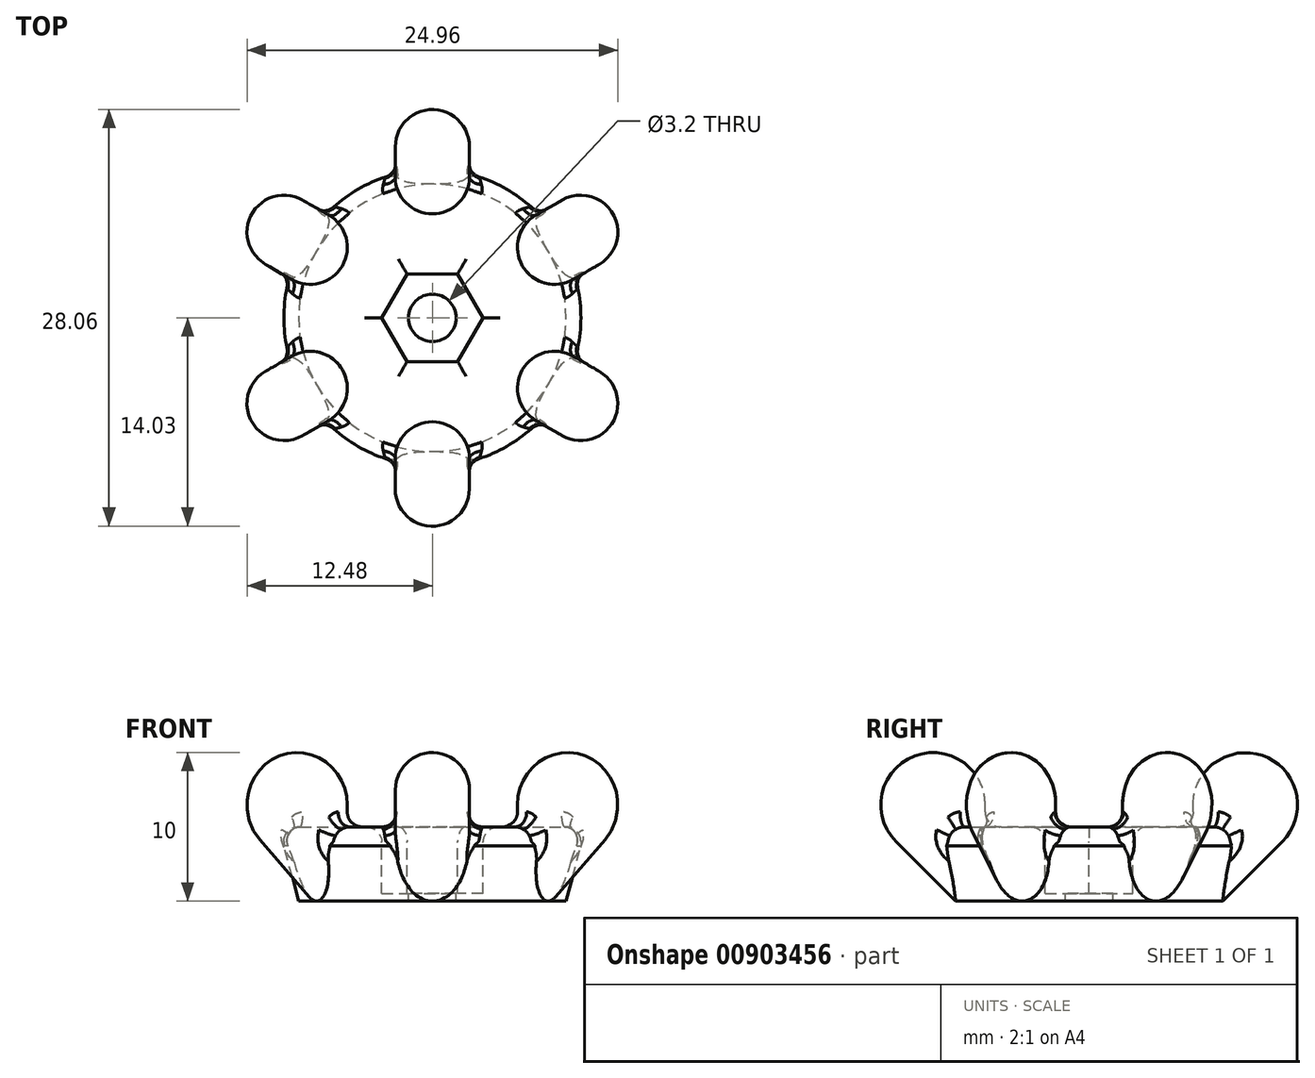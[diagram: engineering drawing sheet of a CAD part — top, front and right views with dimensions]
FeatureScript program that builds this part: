
annotation { "Feature Type Name" : "Feature", "Feature Type Description" : "" }
export const myFeature = defineFeature(function(context is Context, id is Id, definition is map)
    precondition{}
    {
        {
            var Q0;
            Q0=qCreatedBy(makeId("Top.planeOp"),FACE);
            var sketch = newSketch(context, id + "F0", { "sketchPlane" : qUnion([Q0])});
            skCircle(sketch, "E0", {"center": v(0, 0) * mm, "radius": 10 * mm});
            skLineSegment(sketch, "E1", {"start": v(0, 0) * mm, "end": v(0, 13.6) * mm, "construction": true});
            skSolve(sketch);
        }
        {
            var Q0;
            Q0=makeQuery(id+"F0.imprint","IMPRINT",FACE,{"disambiguationData":[TD([[makeQuery(id+"F0.imprint","IMPRINT",EDGE,{"derivedFrom":sQuery(id+"F0.wireOp",EDGE,"E0")}),1.0]])]});
            var Q1;
            Q1=sQuery(id+"F0.wireOp",EDGE,"E1");
            var Q2;
            Q2=sQuery(id+"F0.wireOp",EDGE,"E0");
            extrude(context, id + "F1", {"entities" : qUnion([Q0]), "surfaceEntities" : qUnion([Q1, Q2]), "depth" : 5 * mm, "offsetDistance" : 25 * mm});
        }
        {
            var Q0;
            Q0=makeQuery(id+"F1.opExtrude","CAP_EDGE",EDGE,{"disambiguationData":[OSD([sQuery(id+"F0.wireOp",EDGE,"E0")])],"isStart":true});
            chamfer(context, id + "F2", {"entities" : qUnion([Q0]), "chamferType" : ChamferType.OFFSET_ANGLE, "width" : 1 * mm, "oppositeDirection" : true, "angle" : 75 * degree, "tangentPropagation" : true});
        }
        {
            var Q0;
            Q0=makeQuery(id+"F1.opExtrude","CAP_EDGE",EDGE,{"disambiguationData":[OSD([sQuery(id+"F0.wireOp",EDGE,"E0")])],"isStart":false});
            fillet(context, id + "F3", {"entities" : qUnion([Q0]), "radius" : 1 * mm, "tangentPropagation" : true, "allowEdgeOverflow" : false});
        }
        {
            var Q0;
            Q0=makeQuery(id+"F1.opExtrude","CAP_FACE",FACE,{"disambiguationData":[OSD([sQuery(id+"F0.wireOp",EDGE,"E0")])],"isStart":false});
            var sketch = newSketch(context, id + "F4", { "sketchPlane" : qUnion([Q0])});
            skCircle(sketch, "E2.cCircle", {"center": v(0, 0) * mm, "radius": 2.95 * mm, "construction": true});
            skLineSegment(sketch, "E2.0", {"start": v(-1.7, 2.95) * mm, "end": v(1.7, 2.95) * mm});
            skLineSegment(sketch, "E2.1", {"start": v(1.7, 2.95) * mm, "end": v(3.4, 0) * mm});
            skLineSegment(sketch, "E2.2", {"start": v(3.4, 0) * mm, "end": v(1.7, -2.95) * mm});
            skLineSegment(sketch, "E2.3", {"start": v(1.7, -2.95) * mm, "end": v(-1.7, -2.95) * mm});
            skLineSegment(sketch, "E2.4", {"start": v(-1.7, -2.95) * mm, "end": v(-3.4, 0) * mm});
            skLineSegment(sketch, "E2.5", {"start": v(-3.4, 0) * mm, "end": v(-1.7, 2.95) * mm});
            skPoint(sketch, "E2.0.midPoint", {"position": v(0, 2.95) * mm});
            skCircle(sketch, "E3", {"center": v(0, 0) * mm, "radius": 1.6 * mm});
            skSolve(sketch);
        }
        {
            var Q0;
            Q0=qSketchRegion(id+"F4",true);
            var Q1;
            Q1=makeQuery(id+"F4.imprint","IMPRINT",FACE,{"disambiguationData":[TD([[makeQuery(id+"F4.imprint","IMPRINT",EDGE,{"derivedFrom":sQuery(id+"F4.wireOp",EDGE,"E3")}),1.0]])]});
            extrude(context, id + "F5", {"entities" : qUnion([Q0, Q1]), "operationType" : NewBodyOperationType.REMOVE, "oppositeDirection" : true, "depth" : (5 - 0.5) * mm, "offsetDistance" : 25 * mm});
        }
        {
            var Q0;
            Q0=makeQuery(id+"F4.imprint","IMPRINT",FACE,{"disambiguationData":[TD([[makeQuery(id+"F4.imprint","IMPRINT",EDGE,{"derivedFrom":sQuery(id+"F4.wireOp",EDGE,"E3")}),1.0]])]});
            var Q1;
            Q1=sQuery(id+"F4.wireOp",EDGE,"E3");
            extrude(context, id + "F6", {"entities" : qUnion([Q0]), "operationType" : NewBodyOperationType.REMOVE, "surfaceEntities" : qUnion([Q1]), "oppositeDirection" : true, "depth" : 25 * mm, "offsetDistance" : 25 * mm});
        }
        {
            var Q0;
            Q0=qCreatedBy(makeId("Right.planeOp"),FACE);
            var sketch = newSketch(context, id + "F7", { "sketchPlane" : qUnion([Q0])});
            skLineSegment(sketch, "E4", {"start": v(9, 0) * mm, "end": v(13, 4) * mm});
            skLineSegment(sketch, "E5", {"start": v(7, 2.8) * mm, "end": v(9, 0) * mm});
            skLineSegment(sketch, "E6", {"start": v(-9, 0) * mm, "end": v(-10, 3.73) * mm});
            skLineSegment(sketch, "E7", {"start": v(7, 6.49) * mm, "end": v(7, 2.8) * mm});
            skArc(sketch, "E8", {"start": v(13, 4) * mm, "mid": v(11.86, 9.73) * mm, "end": v(7, 6.49) * mm});
            skLineSegment(sketch, "E9", {"start": v(10, 3.73) * mm, "end": v(9, 0) * mm});
            skPoint(sketch, "E10", {"position": v(10.51, 10) * mm});
            skSolve(sketch);
        }
        {
            var Q0;
            Q0 = qSketchRegion(id + "F7", true);
            extrude(context, id + "F8", {"entities" : qUnion([Q0]), "depth" : 5 * mm, "offsetDistance" : 25 * mm, "symmetric" : true});
        }
        {
            var Q0;
            Q0=makeQuery(id+"F8.opExtrude","CAP_FACE",FACE,{"disambiguationData":[OSD([sQuery(id+"F7.wireOp",EDGE,"E4"),sQuery(id+"F7.wireOp",EDGE,"E5"),sQuery(id+"F7.wireOp",EDGE,"E7"),sQuery(id+"F7.wireOp",EDGE,"E8")])],"isStart":false});
            var Q1;
            Q1=makeQuery(id+"F8.opExtrude","CAP_FACE",FACE,{"disambiguationData":[OSD([sQuery(id+"F7.wireOp",EDGE,"E4"),sQuery(id+"F7.wireOp",EDGE,"E5"),sQuery(id+"F7.wireOp",EDGE,"E7"),sQuery(id+"F7.wireOp",EDGE,"E8")])],"isStart":true});
            fillet(context, id + "F9", {"entities" : qUnion([Q0, Q1]), "radius" : 2.5 * mm, "tangentPropagation" : true, "allowEdgeOverflow" : false});
        }
        {
            var Q0;
            Q0=makeQuery(id+"F8.opExtrude","SWEPT_BODY",BODY,{"disambiguationData":[OSD([sQuery(id+"F7.wireOp",EDGE,"E4"),sQuery(id+"F7.wireOp",EDGE,"E5"),sQuery(id+"F7.wireOp",EDGE,"E7"),sQuery(id+"F7.wireOp",EDGE,"E8")])]});
            var Q1;
            Q1=makeQuery(id+"F3.opFillet","BLEND_FACE",FACE,{"disambiguationData":[OSD([sQuery(id+"F0.wireOp",EDGE,"E0")])]});
            circularPattern(context, id + "F10", {"operationType" : NewBodyOperationType.ADD, "entities" : qUnion([Q0]), "axis" : qUnion([Q1]), "angle" : 360 * degree, "instanceCount" : 6, "equalSpace" : true});
        }
        {
            var Q0;
            Q0=makeQuery(id+"F1.opExtrude","CAP_FACE",FACE,{"disambiguationData":[OSD([sQuery(id+"F0.wireOp",EDGE,"E0")])],"isStart":false});
            fillet(context, id + "F11", {"entities" : qUnion([Q0]), "radius" : 1 * mm, "tangentPropagation" : true, "allowEdgeOverflow" : false});
        }
    });
